# Revit family: STARC-REALWALL-NEGATIVE AIR PANEL
name_source: partatom
category: Specialty Equipment
revit_build: Autodesk Revit 2014 (Build: 20140709_2115(x64)
units: mm (PartAtom-declared; Revit-internal decimal feet)

## types (4) — shared parameters
ASTM Standard = E-84 CLASS A
Assembly Code = F1030900
Ceiling Height = 9' - 0"
Description = STARC SYSTEMS, INC REALWALL TEMPORARY CONTAINMENT SYSTEM NEGATIVE AIR PANEL
Height = 9' - 0"
ICRA Class = IV
Manufacturer = STARC SYSTEMS, INC.
URL = https://starcsystems.com

## per-type parameters (varying)
| type | Type Comments | Width |
| S3-AIR-24 | STARC REALWALL 24 INCH NEGATIVE AIR PANEL | 2' - 0" |
| S3-AIR-32 | STARC REALWALL 32 INCH NEGATIVE AIR PANEL | 2' - 8" |
| S3-AIR-18 | STARC REALWALL 18 INCH NEGATIVE AIR PANEL | 1' - 6" |
| S3-AIR-42 | STARC REALWALL 42 INCH NEGATIVE AIR PANEL | 3' - 6" |

note: column(s) folded — value = type name in every type: Model

## geometry (parser evidence)
native form markers: Sweep x14
no freeform markers — native parametric forms only
